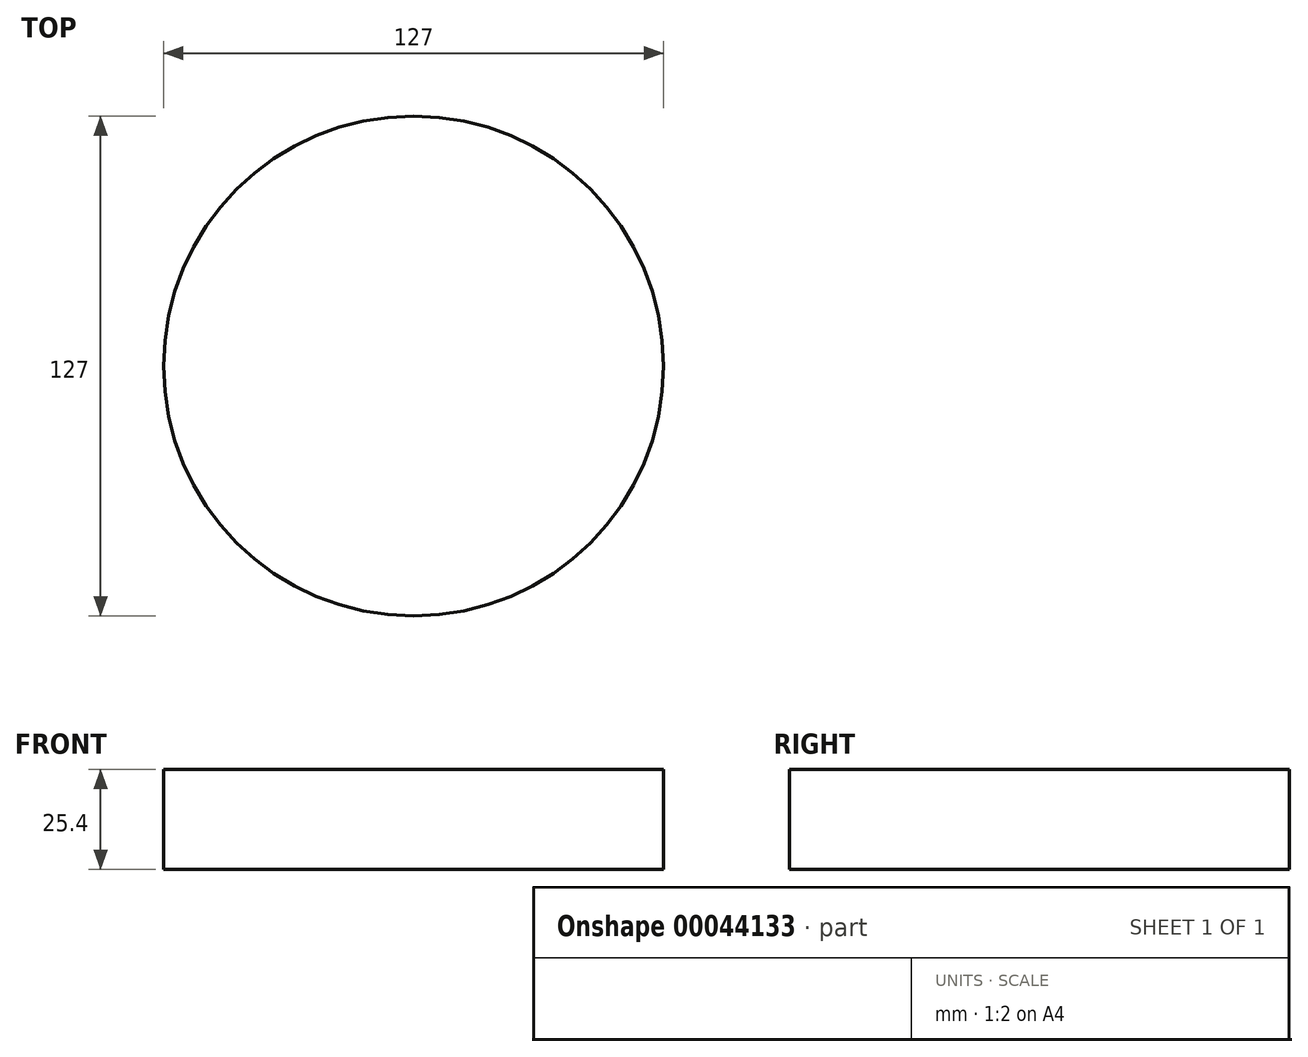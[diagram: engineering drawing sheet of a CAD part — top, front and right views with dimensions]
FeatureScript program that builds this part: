
annotation { "Feature Type Name" : "Feature", "Feature Type Description" : "" }
export const myFeature = defineFeature(function(context is Context, id is Id, definition is map)
    precondition{}
    {
        {
            var Q0;
            Q0=qCreatedBy(makeId("Top.planeOp"),FACE);
            var sketch = newSketch(context, id + "F0", { "sketchPlane" : qUnion([Q0])});
            skCircle(sketch, "E0", {"center": v(0, 0) * mm, "radius": 63.5 * mm});
            skSolve(sketch);
        }
        {
            var Q0;
            Q0=makeQuery(id+"F0.imprint","IMPRINT",FACE,{"disambiguationData":[TD([[makeQuery(id+"F0.imprint","IMPRINT",EDGE,{"derivedFrom":sQuery(id+"F0.wireOp",EDGE,"E0")}),1.0]])]});
            extrude(context, id + "F1", {"entities" : qUnion([Q0]), "depth" : 25.4 * mm});
        }
    });
